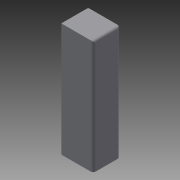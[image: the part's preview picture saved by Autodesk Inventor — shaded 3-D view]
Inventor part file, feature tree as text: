
AUTODESK INVENTOR PART (.ipt)
format: ipt  version: 2016 (Build 200138000, 138)  size: 79,360 bytes
history: native  units: mm
features: extrude x1, fillet x1, sketch x1
ambient origin geometry x8: Origin, YZ Plane, XZ Plane, XY Plane, X Axis, Y Axis, Z Axis, Center Point
bodies: Solid1 (feature_tree)
feature tree (3):
  extrude  "Extrusion1"  Depth=97.0mm
  fillet  "Fillet1"  Radius=23.0mm
  sketch  "Sketch1"  dims[d0=28.4mm d1=97.0mm d2=23.0mm d3=0.0mm d4=2.0mm]
